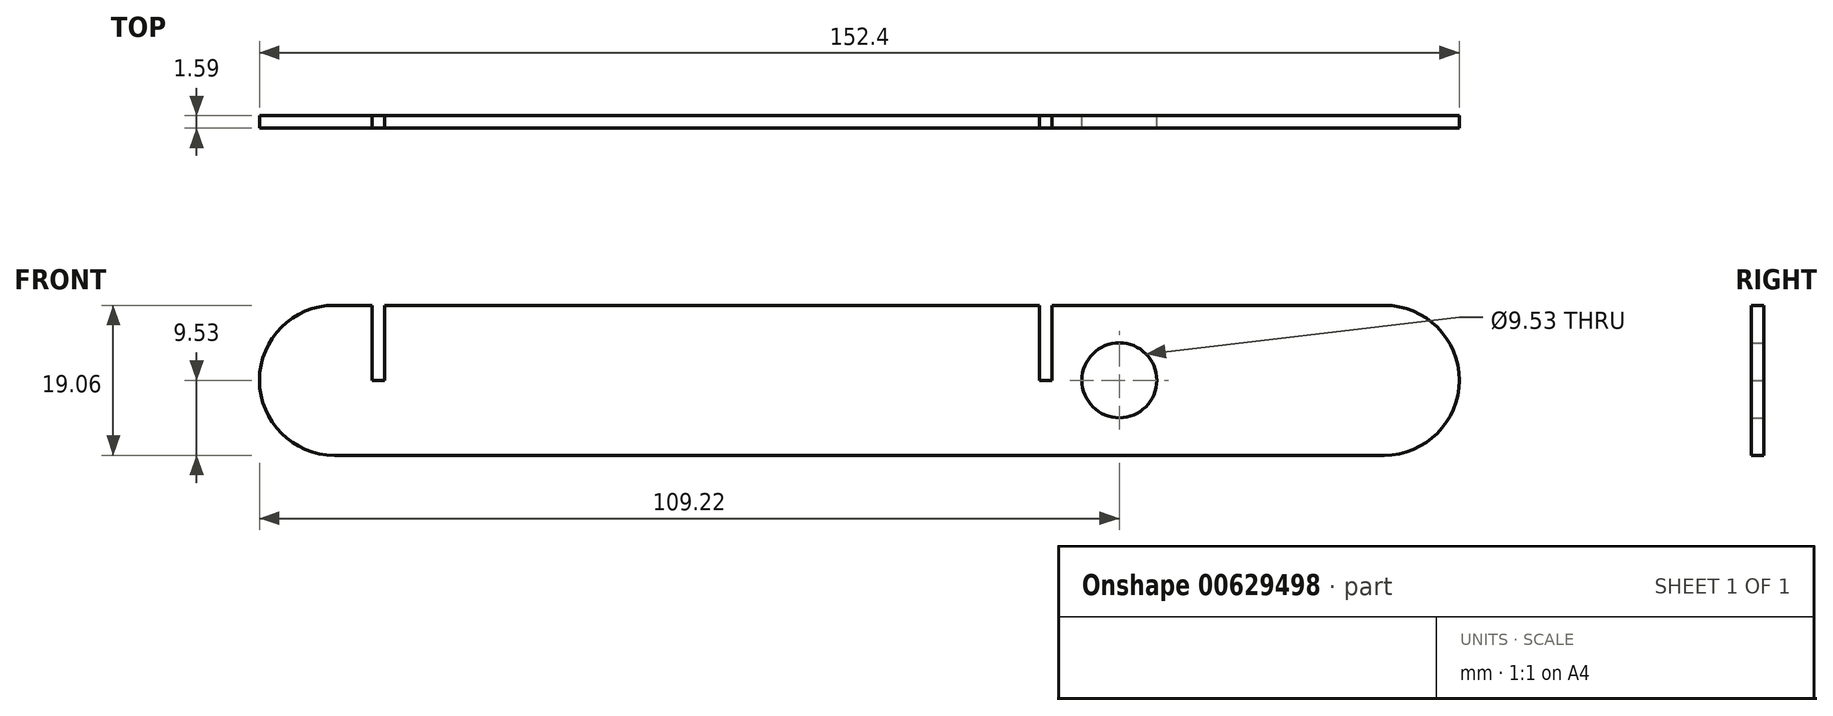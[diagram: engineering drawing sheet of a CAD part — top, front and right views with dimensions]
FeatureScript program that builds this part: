
annotation { "Feature Type Name" : "Feature", "Feature Type Description" : "" }
export const myFeature = defineFeature(function(context is Context, id is Id, definition is map)
    precondition{}
    {
        {
            var Q0;
            Q0=qCreatedBy(makeId("Front.planeOp"),FACE);
            var sketch = newSketch(context, id + "F0", { "sketchPlane" : qUnion([Q0])});
            skLineSegment(sketch, "E0.bottom", {"start": v(66.68, -9.52) * mm, "end": v(-66.68, -9.52) * mm});
            skLineSegment(sketch, "E0.top", {"start": v(66.68, 9.52) * mm, "end": v(-66.68, 9.52) * mm});
            skPoint(sketch, "E0.middle", {"position": v(0, 0) * mm});
            skArc(sketch, "E1", {"start": v(-66.68, 9.52) * mm, "mid": v(-76.2, 0) * mm, "end": v(-66.68, -9.52) * mm});
            skArc(sketch, "E2", {"start": v(66.68, -9.52) * mm, "mid": v(76.2, 0) * mm, "end": v(66.68, 9.52) * mm});
            skLineSegment(sketch, "E3", {"start": v(-61.91, 9.52) * mm, "end": v(-61.91, 0) * mm});
            skLineSegment(sketch, "E4", {"start": v(-61.91, 0) * mm, "end": v(-60.33, 0) * mm});
            skLineSegment(sketch, "E5", {"start": v(-60.33, 0) * mm, "end": v(-60.33, 9.52) * mm});
            skLineSegment(sketch, "E6", {"start": v(0, 0) * mm, "end": v(66.68, 0) * mm, "construction": true});
            skCircle(sketch, "E7", {"center": v(33.02, 0) * mm, "radius": 4.76 * mm});
            skLineSegment(sketch, "E8.bottom", {"start": v(24.45, 9.52) * mm, "end": v(22.86, 9.52) * mm});
            skLineSegment(sketch, "E8.top", {"start": v(24.45, 0) * mm, "end": v(22.86, 0) * mm});
            skLineSegment(sketch, "E8.left", {"start": v(24.45, 9.52) * mm, "end": v(24.45, 0) * mm});
            skLineSegment(sketch, "E8.right", {"start": v(22.86, 9.52) * mm, "end": v(22.86, 0) * mm});
            skSolve(sketch);
        }
        {
            var Q0;
            Q0=makeQuery(id+"F0.imprint","IMPRINT",FACE,{"disambiguationData":[TD([[makeQuery(id+"F0.imprint","IMPRINT",EDGE,{"derivedFrom":sQuery(id+"F0.wireOp",EDGE,"E0.bottom")}),-1.0]])]});
            extrude(context, id + "F1", {"entities" : qUnion([Q0]), "depth" : 1.59 * mm, "offsetDistance" : 25.4 * mm});
        }
    });
